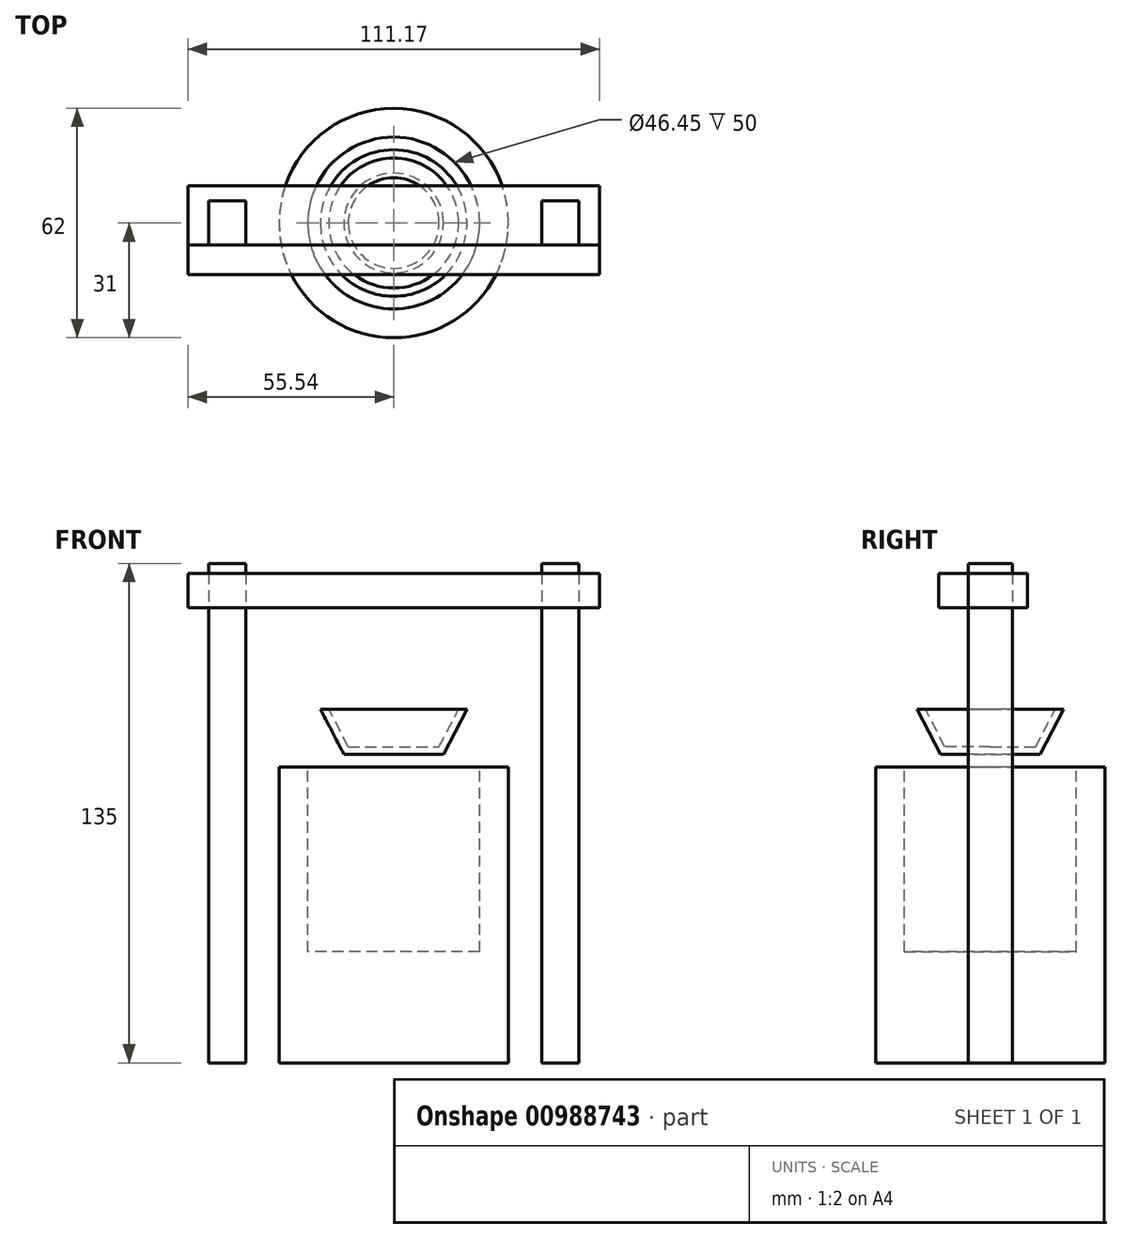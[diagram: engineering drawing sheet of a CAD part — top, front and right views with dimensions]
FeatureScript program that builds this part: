
annotation { "Feature Type Name" : "Feature", "Feature Type Description" : "" }
export const myFeature = defineFeature(function(context is Context, id is Id, definition is map)
    precondition{}
    {
        {
            var Q0;
            Q0=qCreatedBy(makeId("Top.planeOp"),FACE);
            var sketch = newSketch(context, id + "F0", { "sketchPlane" : qUnion([Q0])});
            skCircle(sketch, "E0", {"center": v(0, 0) * mm, "radius": 31 * mm});
            skSolve(sketch);
        }
        {
            var Q0;
            Q0 = qSketchRegion(id + "F0", true);
            extrude(context, id + "F1", {"entities" : qUnion([Q0]), "depth" : 80 * mm, "offsetDistance" : 25 * mm});
        }
        {
            var Q0;
            Q0=makeQuery(id+"F1.opExtrude","CAP_FACE",FACE,{"disambiguationData":[OSD([sQuery(id+"F0.wireOp",EDGE,"E0")])],"isStart":false});
            var sketch = newSketch(context, id + "F2", { "sketchPlane" : qUnion([Q0])});
            skCircle(sketch, "E1", {"center": v(0, 0) * mm, "radius": 23.23 * mm});
            skSolve(sketch);
        }
        {
            var Q0;
            Q0=qCreatedBy(makeId("Top.planeOp"),FACE);
            var sketch = newSketch(context, id + "F3", { "sketchPlane" : qUnion([Q0])});
            skLineSegment(sketch, "E2.bottom", {"start": v(-50.03, 6) * mm, "end": v(-40, 6) * mm});
            skLineSegment(sketch, "E2.top", {"start": v(-50.03, -6) * mm, "end": v(-40, -6) * mm});
            skLineSegment(sketch, "E2.left", {"start": v(-50.03, 6) * mm, "end": v(-50.03, -6) * mm});
            skLineSegment(sketch, "E2.right", {"start": v(-40, 6) * mm, "end": v(-40, -6) * mm});
            skSolve(sketch);
        }
        {
            var Q0;
            Q0 = qSketchRegion(id + "F3", true);
            extrude(context, id + "F4", {"entities" : qUnion([Q0]), "depth" : 135 * mm, "offsetDistance" : 25 * mm});
        }
        {
            var Q0;
            Q0=makeQuery(id+"F4.opExtrude","SWEPT_BODY",BODY,{"disambiguationData":[OSD([sQuery(id+"F3.wireOp",EDGE,"E2.bottom"),sQuery(id+"F3.wireOp",EDGE,"E2.top"),sQuery(id+"F3.wireOp",EDGE,"E2.left"),sQuery(id+"F3.wireOp",EDGE,"E2.right")])]});
            var Q1;
            Q1=qCreatedBy(makeId("Right.planeOp"),FACE);
            mirror(context, id + "F5", {"entities" : qUnion([Q0]), "mirrorPlane" : qUnion([Q1])});
        }
        {
            var Q0;
            Q0 = qSketchRegion(id + "F2", true);
            extrude(context, id + "F6", {"entities" : qUnion([Q0]), "operationType" : NewBodyOperationType.REMOVE, "oppositeDirection" : true, "depth" : 50 * mm, "offsetDistance" : 25 * mm});
        }
        {
            var Q0;
            Q0=makeQuery(id+"F4.opExtrude","SWEPT_FACE",FACE,{"disambiguationData":[OSD([sQuery(id+"F3.wireOp",EDGE,"E2.top")])]});
            var sketch = newSketch(context, id + "F7", { "sketchPlane" : qUnion([Q0])});
            skLineSegment(sketch, "E3.bottom", {"start": v(-55.54, 132.3) * mm, "end": v(55.63, 132.3) * mm});
            skLineSegment(sketch, "E3.top", {"start": v(-55.54, 123.04) * mm, "end": v(55.63, 123.04) * mm});
            skLineSegment(sketch, "E3.left", {"start": v(-55.54, 132.3) * mm, "end": v(-55.54, 123.04) * mm});
            skLineSegment(sketch, "E3.right", {"start": v(55.63, 132.3) * mm, "end": v(55.63, 123.04) * mm});
            skSolve(sketch);
        }
        {
            var Q0;
            Q0 = qSketchRegion(id + "F7", true);
            extrude(context, id + "F8", {"entities" : qUnion([Q0]), "operationType" : NewBodyOperationType.ADD, "depth" : 8 * mm, "offsetDistance" : 25 * mm});
        }
        {
            var Q0;
            Q0 = qSketchRegion(id + "F7", true);
            extrude(context, id + "F9", {"entities" : qUnion([Q0]), "depth" : -16 * mm, "offsetDistance" : 25 * mm});
        }
        {
            var Q0;
            Q0=qCreatedBy(makeId("Front.planeOp"),FACE);
            var sketch = newSketch(context, id + "F10", { "sketchPlane" : qUnion([Q0])});
            skLineSegment(sketch, "E4", {"start": v(0, 83.43) * mm, "end": v(-13.48, 83.43) * mm});
            skLineSegment(sketch, "E5", {"start": v(-13.48, 83.43) * mm, "end": v(-19.81, 95.6) * mm});
            skLineSegment(sketch, "E6", {"start": v(-19.81, 95.6) * mm, "end": v(0, 95.6) * mm});
            skLineSegment(sketch, "E7", {"start": v(0, 95.6) * mm, "end": v(0, 83.43) * mm});
            skPoint(sketch, "E8.start.orphan", {"position": v(16.2, 95.94) * mm});
            skPoint(sketch, "E9.trimOffspring.end.orphan", {"position": v(16.2, 95.6) * mm});
            skSolve(sketch);
        }
        {
            var Q0;
            Q0=makeQuery(id+"F10.imprint","IMPRINT",FACE,{"disambiguationData":[TD([[makeQuery(id+"F10.imprint","IMPRINT",EDGE,{"derivedFrom":sQuery(id+"F10.wireOp",EDGE,"E4")}),-1.0]])]});
            var sketch = newSketch(context, id + "F11", { "sketchPlane" : qUnion([Q0])});
            skLineSegment(sketch, "E10", {"start": v(0, 96.6) * mm, "end": v(0, 99.96) * mm});
            skSolve(sketch);
        }
        {
            var Q0;
            Q0=makeQuery(id+"F10.imprint","IMPRINT",FACE,{"disambiguationData":[TD([[makeQuery(id+"F10.imprint","IMPRINT",EDGE,{"derivedFrom":sQuery(id+"F10.wireOp",EDGE,"E4")}),-1.0]])]});
            var Q1;
            Q1=sQuery(id+"F11.wireOp",EDGE,"E10");
            revolve(context, id + "F12", {"surfaceOperationType" : NewSurfaceOperationType.NEW, "entities" : qUnion([Q0]), "axis" : qUnion([Q1]), "revolveType" : RevolveType.FULL});
        }
        {
            var Q0;
            Q0=makeQuery(id+"F12.opRevolve","SWEPT_FACE",FACE,{"disambiguationData":[OSD([sQuery(id+"F10.wireOp",EDGE,"E6")])]});
            shell(context, id + "F13", {"entities" : qUnion([Q0]), "thickness" : 2 * mm});
        }
    });
